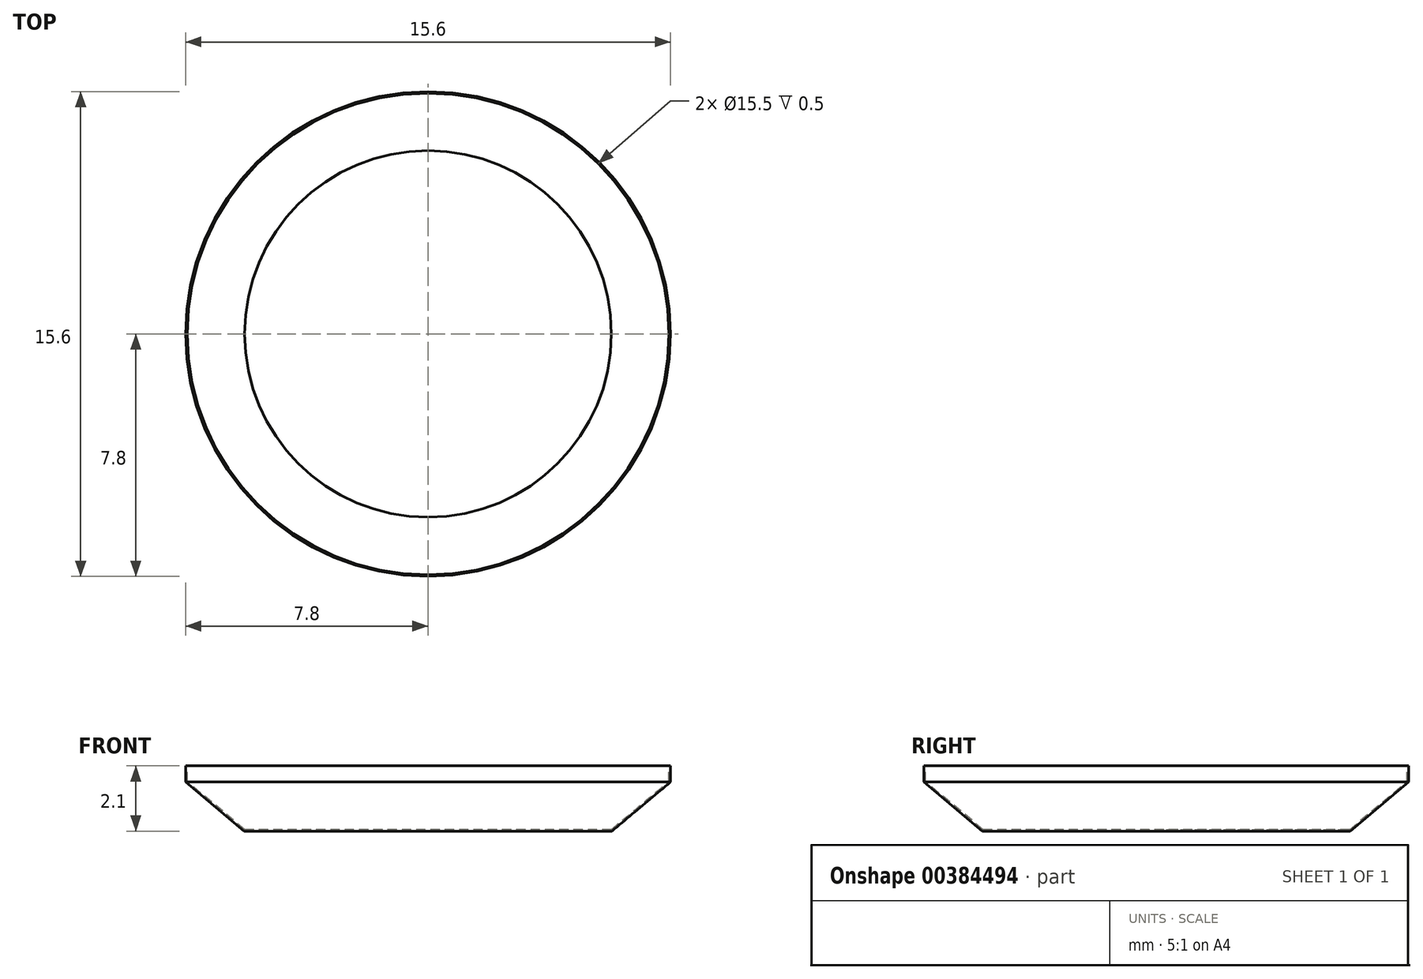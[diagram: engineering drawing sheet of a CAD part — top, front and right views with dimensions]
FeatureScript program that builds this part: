
annotation { "Feature Type Name" : "Feature", "Feature Type Description" : "" }
export const myFeature = defineFeature(function(context is Context, id is Id, definition is map)
    precondition{}
    {
        {
            var Q0;
            Q0=qCreatedBy(makeId("Front.planeOp"),FACE);
            var sketch = newSketch(context, id + "F0", { "sketchPlane" : qUnion([Q0])});
            skLineSegment(sketch, "E0", {"start": v(0, 13.95) * mm, "end": v(0, 0) * mm, "construction": true});
            skLineSegment(sketch, "E1", {"start": v(0, 0) * mm, "end": v(5.9, 0) * mm});
            skLineSegment(sketch, "E2", {"start": v(5.9, 0) * mm, "end": v(7.75, 1.55) * mm});
            skLineSegment(sketch, "E3", {"start": v(7.75, 1.55) * mm, "end": v(7.75, 2.05) * mm});
            skLineSegment(sketch, "E4.1", {"start": v(5.9, 0) * mm, "end": v(7.76, 1.55) * mm});
            skLineSegment(sketch, "E5.0", {"start": v(7.8, 1.53) * mm, "end": v(7.8, 2.05) * mm});
            skLineSegment(sketch, "E5.1", {"start": v(5.92, -0.05) * mm, "end": v(7.8, 1.53) * mm});
            skLineSegment(sketch, "E5.2", {"start": v(0, -0.05) * mm, "end": v(5.92, -0.05) * mm});
            skLineSegment(sketch, "E6", {"start": v(7.75, 2.05) * mm, "end": v(7.8, 2.05) * mm});
            skLineSegment(sketch, "E7", {"start": v(0, 0) * mm, "end": v(0, -0.05) * mm});
            skSolve(sketch);
        }
        {
            var Q0;
            Q0 = qSketchRegion(id + "F0", true);
            var Q1;
            Q1=sQuery(id+"F0.wireOp",EDGE,"E0");
            revolve(context, id + "F1", {"entities" : qUnion([Q0]), "axis" : qUnion([Q1]), "revolveType" : RevolveType.FULL});
        }
    });
